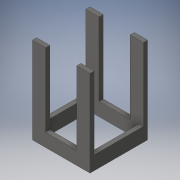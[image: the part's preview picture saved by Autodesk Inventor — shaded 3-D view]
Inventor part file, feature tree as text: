
AUTODESK INVENTOR PART (.ipt)
format: ipt  version: 2016 SP1 (Build 200210100, 210)  size: 140,288 bytes
history: native  units: in
note: dims shown in document units (in); Inventor stores cm internally (conversion verified against a paired STEP export)
features: extrude x3, sketch x3
ambient origin geometry x8: Origin, YZ Plane, XZ Plane, XY Plane, X Axis, Y Axis, Z Axis, Center Point
bodies: Solid1 (feature_tree)
feature tree (6):
  extrude  "Extrusion1"  Depth=24.0in
  extrude  "Extrusion2"  Depth=5.5in
  extrude  "Extrusion3"  Depth=5.5in
  sketch  "Sketch1"  dims[d0=24.0in d1=24.0in]
  sketch  "Sketch2"  dims[d2=1.75in d3=5.5in]
  sketch  "Sketch3"  dims[d4=36.0in d5=0.0in d6=5.5in d7=36.0in d8=0.0in d9=1.75in d10=36.0in d11=0.0in]
